# Revit family: Acrytec Panel - Gemtex
name_source: partatom
category: Generic Models
revit_build: Autodesk Revit 2016 (Build: 20150220_1215(x64)
units: mm (PartAtom-declared; Revit-internal decimal feet)

## family parameters
Always vertical = Yes
Can host rebar = No
Cut with Voids When Loaded = No
Part Type = Normal
Room Calculation Point = No
Round Connector Dimension = Use Diameter
Shared = No
Work Plane-Based = No

## types (1)
- Acrytec Panel - Gemtex
    Aqua = No
    Arctic Snow = No
    Blue Sky = Yes
    Capstone = No
    Caramel = No
    Chipped Ice = No
    Cookie Dough = No
    Copper Brown = No
    Desert Stone = No
    Egg Plant = No
    Granite = No
    Insulated Panel Type = Yes
    Midnight = No
    Oakville Clay = No
    Ocean Spray = No
    Panel-A-CL-Offset = 383 mm
    Pepper = No
    Rocky Road = No
    Rustic = No
    Slate Grey = No
    Tuxedo Black = No
    Uninsulated Panel Type = No
    Vanilla = No

## geometry (parser evidence)
native form markers: Blend x4, Sweep x23
no freeform markers — native parametric forms only
